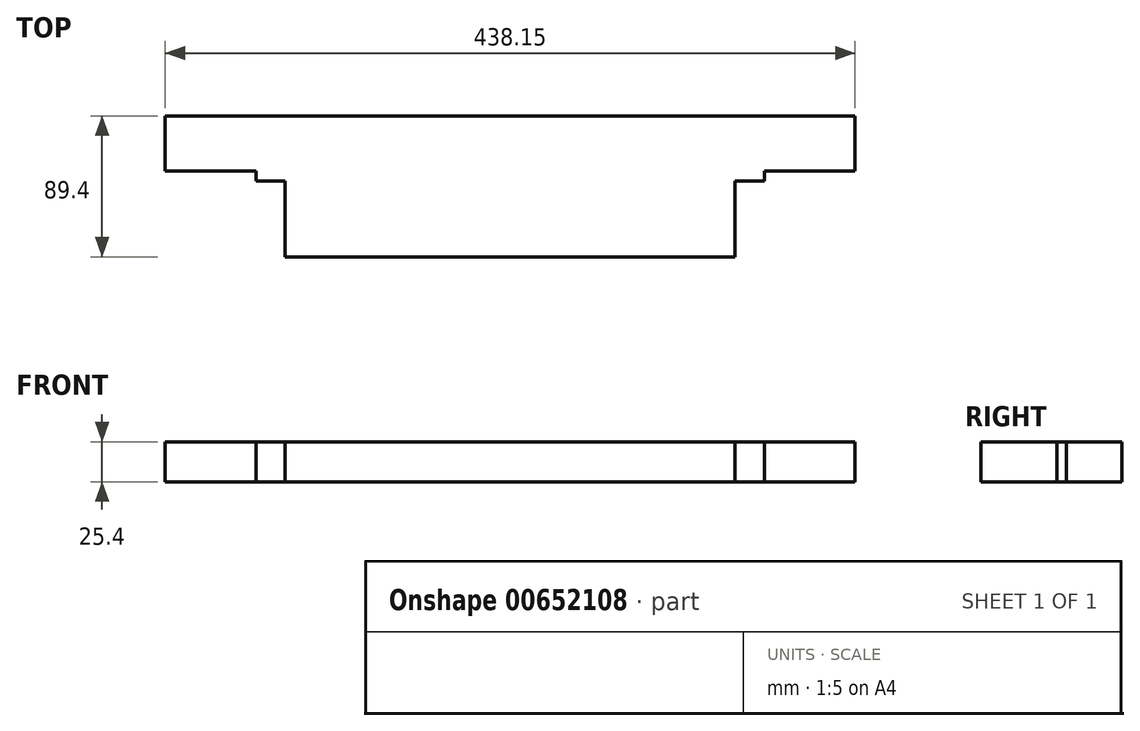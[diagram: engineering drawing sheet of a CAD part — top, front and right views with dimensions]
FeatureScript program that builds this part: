
annotation { "Feature Type Name" : "Feature", "Feature Type Description" : "" }
export const myFeature = defineFeature(function(context is Context, id is Id, definition is map)
    precondition{}
    {
        {
            var Q0;
            Q0=qCreatedBy(makeId("Top.planeOp"),FACE);
            var sketch = newSketch(context, id + "F0", { "sketchPlane" : qUnion([Q0])});
            skLineSegment(sketch, "E0.top", {"start": v(-285.75, -27.12) * mm, "end": v(0, -27.12) * mm});
            skLineSegment(sketch, "E0.left", {"start": v(-285.75, 21.14) * mm, "end": v(-285.75, -27.12) * mm});
            skLineSegment(sketch, "E0.right", {"start": v(0, 21.14) * mm, "end": v(0, -27.12) * mm});
            skLineSegment(sketch, "E1", {"start": v(-285.75, 21.14) * mm, "end": v(-304.3, 21.14) * mm});
            skLineSegment(sketch, "E2", {"start": v(-304.3, 21.14) * mm, "end": v(-304.3, 27.23) * mm});
            skLineSegment(sketch, "E3", {"start": v(18.54, 27.23) * mm, "end": v(18.54, 21.14) * mm});
            skLineSegment(sketch, "E4", {"start": v(18.54, 21.14) * mm, "end": v(0, 21.14) * mm});
            skLineSegment(sketch, "E5", {"start": v(-304.3, 27.23) * mm, "end": v(-361.95, 27.23) * mm});
            skLineSegment(sketch, "E6", {"start": v(-361.95, 27.23) * mm, "end": v(-361.95, 62.28) * mm});
            skLineSegment(sketch, "E7", {"start": v(-361.95, 62.28) * mm, "end": v(76.2, 62.28) * mm});
            skLineSegment(sketch, "E8", {"start": v(76.2, 62.28) * mm, "end": v(76.2, 27.23) * mm});
            skLineSegment(sketch, "E9", {"start": v(76.2, 27.23) * mm, "end": v(18.54, 27.23) * mm});
            skSolve(sketch);
        }
        {
            var Q0;
            Q0=makeQuery(id+"F0.imprint","IMPRINT",FACE,{"disambiguationData":[TD([[makeQuery(id+"F0.imprint","IMPRINT",EDGE,{"derivedFrom":sQuery(id+"F0.wireOp",EDGE,"E0.top")}),1.0]])]});
            extrude(context, id + "F1", {"entities" : qUnion([Q0]), "depth" : 25.4 * mm, "offsetDistance" : 25.4 * mm});
        }
    });
